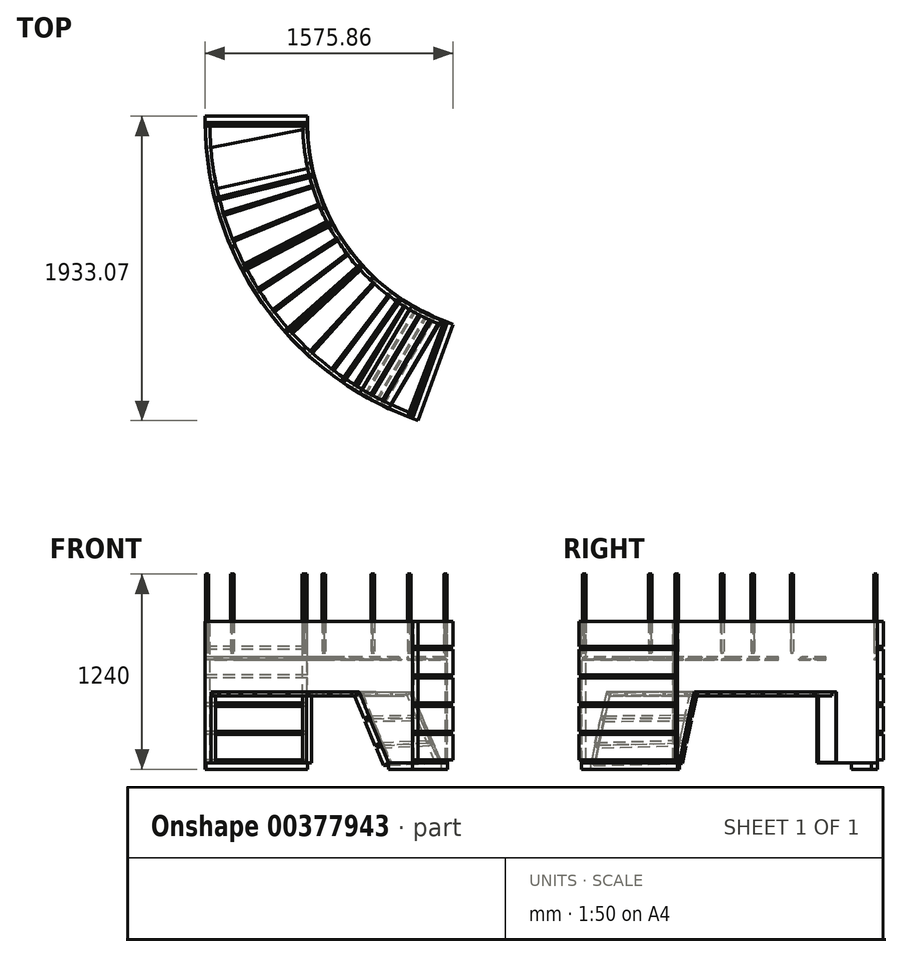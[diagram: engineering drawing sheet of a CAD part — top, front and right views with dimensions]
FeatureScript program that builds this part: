
annotation { "Feature Type Name" : "Feature", "Feature Type Description" : "" }
export const myFeature = defineFeature(function(context is Context, id is Id, definition is map)
    precondition{}
    {
        {
            var Q0;
            Q0=qCreatedBy(makeId("Front.planeOp"),FACE);
            var sketch = newSketch(context, id + "F0", { "sketchPlane" : qUnion([Q0])});
            skLineSegment(sketch, "E0", {"start": v(0, 0) * mm, "end": v(0, -500) * mm, "construction": true});
            skSolve(sketch);
        }
        {
            var Q0;
            Q0=qCreatedBy(makeId("Front.planeOp"),FACE);
            var sketch = newSketch(context, id + "F1", { "sketchPlane" : qUnion([Q0])});
            skLineSegment(sketch, "E1.bottom", {"start": v(-1350, 0) * mm, "end": v(-1380, 0) * mm});
            skLineSegment(sketch, "E1.top", {"start": v(-1350, 900) * mm, "end": v(-1380, 900) * mm});
            skLineSegment(sketch, "E1.left", {"start": v(-1350, 0) * mm, "end": v(-1350, 900) * mm});
            skLineSegment(sketch, "E1.right", {"start": v(-1380, 0) * mm, "end": v(-1380, 900) * mm});
            skLineSegment(sketch, "E2.bottom", {"start": v(-1970, 0) * mm, "end": v(-2000, 0) * mm});
            skLineSegment(sketch, "E2.top", {"start": v(-1970, 900) * mm, "end": v(-2000, 900) * mm});
            skLineSegment(sketch, "E2.left", {"start": v(-1970, 0) * mm, "end": v(-1970, 900) * mm});
            skLineSegment(sketch, "E2.right", {"start": v(-2000, 0) * mm, "end": v(-2000, 900) * mm});
            skSolve(sketch);
        }
        {
            var Q0;
            Q0=qCreatedBy(makeId("Top.planeOp"),FACE);
            var sketch = newSketch(context, id + "F2", { "sketchPlane" : qUnion([Q0])});
            skLineSegment(sketch, "E3", {"start": v(0, 0) * mm, "end": v(-461.73, -1268.59) * mm, "construction": true});
            skLineSegment(sketch, "E4", {"start": v(0, 0) * mm, "end": v(-1350, 0) * mm, "construction": true});
            skArc(sketch, "E5", {"start": v(-1350, 0) * mm, "mid": v(-1105.86, -774.33) * mm, "end": v(-461.73, -1268.59) * mm});
            skSolve(sketch);
        }
        {
            var Q0;
            Q0 = qSketchRegion(id + "F1", true);
            var Q1;
            Q1 = qConstructionFilter(qBodyType(qCreatedBy(id + "F2" ,EDGE), BodyType.WIRE), ConstructionObject.NO);
            sweep(context, id + "F3", {"profiles" : qUnion([Q0]), "path" : qUnion([Q1])});
        }
        {
            var Q0;
            Q0=qCreatedBy(makeId("Top.planeOp"),FACE);
            var sketch = newSketch(context, id + "F4", { "sketchPlane" : qUnion([Q0])});
            skLineSegment(sketch, "E6", {"start": v(0, 0) * mm, "end": v(-2454.07, -477.02) * mm});
            skLineSegment(sketch, "E7", {"start": v(-2454.07, -477.02) * mm, "end": v(-1287.6, -2142.92) * mm});
            skLineSegment(sketch, "E8", {"start": v(-1287.6, -2142.92) * mm, "end": v(0, 0) * mm});
            skSolve(sketch);
        }
        {
            var Q0;
            Q0 = qSketchRegion(id + "F4", true);
            extrude(context, id + "F5", {"entities" : qUnion([Q0]), "operationType" : NewBodyOperationType.REMOVE, "depth" : 450 * mm});
        }
        {
            var Q0;
            {var subQ0=sQuery(id+"F4.wireOp",EDGE,"E8");Q0=makeQuery(id+"F5.boolean.opBoolean","COPY",EDGE,{"disambiguationData":[topologyDisambiguationEdgeConnected([makeQuery(id+"F3.opSweep","SWEPT_FACE",FACE,{"disambiguationData":[OSD([sQuery(id+"F1.wireOp",EDGE,"E2.bottom"),sQuery(id+"F2.wireOp",EDGE,"E5")])]})])],"derivedFrom":makeQuery(id+"F5.opExtrude","CAP_EDGE",EDGE,{"disambiguationData":[OSD([subQ0])],"isStart":true})});}
            var Q1;
            {var subQ0=sQuery(id+"F4.wireOp",EDGE,"E8");Q1=makeQuery(id+"F5.boolean.opBoolean","COPY",EDGE,{"disambiguationData":[topologyDisambiguationEdgeConnected([makeQuery(id+"F3.opSweep","SWEPT_FACE",FACE,{"disambiguationData":[OSD([sQuery(id+"F1.wireOp",EDGE,"E1.bottom"),sQuery(id+"F2.wireOp",EDGE,"E5")])]})])],"derivedFrom":makeQuery(id+"F5.opExtrude","CAP_EDGE",EDGE,{"disambiguationData":[OSD([subQ0])],"isStart":true})});}
            var Q2;
            {var subQ0=sQuery(id+"F4.wireOp",EDGE,"E6");Q2=makeQuery(id+"F5.boolean.opBoolean","COPY",EDGE,{"disambiguationData":[topologyDisambiguationEdgeConnected([makeQuery(id+"F3.opSweep","SWEPT_FACE",FACE,{"disambiguationData":[OSD([sQuery(id+"F1.wireOp",EDGE,"E1.bottom"),sQuery(id+"F2.wireOp",EDGE,"E5")])]})])],"derivedFrom":makeQuery(id+"F5.opExtrude","CAP_EDGE",EDGE,{"disambiguationData":[OSD([subQ0])],"isStart":true})});}
            var Q3;
            {var subQ0=sQuery(id+"F4.wireOp",EDGE,"E6");Q3=makeQuery(id+"F5.boolean.opBoolean","COPY",EDGE,{"disambiguationData":[topologyDisambiguationEdgeConnected([makeQuery(id+"F3.opSweep","SWEPT_FACE",FACE,{"disambiguationData":[OSD([sQuery(id+"F1.wireOp",EDGE,"E2.bottom"),sQuery(id+"F2.wireOp",EDGE,"E5")])]})])],"derivedFrom":makeQuery(id+"F5.opExtrude","CAP_EDGE",EDGE,{"disambiguationData":[OSD([subQ0])],"isStart":true})});}
            chamfer(context, id + "F6", {"entities" : qUnion([Q0, Q1, Q2, Q3]), "chamferType" : ChamferType.OFFSET_ANGLE, "width" : 220 * mm, "oppositeDirection" : false, "angle" : 65 * degree, "tangentPropagation" : true});
        }
        {
            var Q0;
            Q0=makeQuery(id+"F3.opSweep","SWEPT_FACE",FACE,{"disambiguationData":[OSD([sQuery(id+"F1.wireOp",EDGE,"E2.left"),sQuery(id+"F2.wireOp",EDGE,"E5")])]});
            var Q1;
            Q1=makeQuery(id+"F3.opSweep","SWEPT_FACE",FACE,{"disambiguationData":[OSD([sQuery(id+"F1.wireOp",EDGE,"E2.top"),sQuery(id+"F2.wireOp",EDGE,"E5")])]});
            var Q2;
            Q2=makeQuery(id+"F3.opSweep","SWEPT_FACE",FACE,{"disambiguationData":[OSD([sQuery(id+"F1.wireOp",EDGE,"E1.right"),sQuery(id+"F2.wireOp",EDGE,"E5")])]});
            var Q3;
            Q3=makeQuery(id+"F3.opSweep","SWEPT_FACE",FACE,{"disambiguationData":[OSD([sQuery(id+"F1.wireOp",EDGE,"E1.top"),sQuery(id+"F2.wireOp",EDGE,"E5")])]});
            shell(context, id + "F7", {"entities" : qUnion([Q0, Q1, Q2, Q3]), "thickness" : 2.5 * mm});
        }
        {
            var Q0;
            {var subQ0=sQuery(id+"F2.wireOp",EDGE,"E5");var subQ1=sQuery(id+"F4.wireOp",EDGE,"E6");var subQ2=sQuery(id+"F4.wireOp",EDGE,"E8");Q0=makeQuery(id+"F5.boolean.opBoolean","COPY",FACE,{"disambiguationData":[TD([makeQuery(id+"F3.opSweep","SWEPT_FACE",FACE,{"disambiguationData":[OSD([sQuery(id+"F1.wireOp",EDGE,"E1.left"),subQ0])]})])],"derivedFrom":makeQuery(id+"F5.opExtrude","CAP_FACE",FACE,{"disambiguationData":[OSD([subQ1,sQuery(id+"F4.wireOp",EDGE,"E7"),subQ2])],"isStart":false})});}
            var Q1;
            Q1=makeQuery(id+"F3.opSweep","SWEPT_FACE",FACE,{"disambiguationData":[OSD([sQuery(id+"F1.wireOp",EDGE,"E1.top"),sQuery(id+"F2.wireOp",EDGE,"E5")])]});
            cPlane(context, id + "F8", {"entities" : qUnion([Q0, Q1]), "cplaneType" : CPlaneType.MID_PLANE, "offset" : 25 * mm, "width" : 150 * mm, "height" : 150 * mm});
        }
        {
            var Q0;
            Q0=qCreatedBy(id+"F8.planeOp",FACE);
            var sketch = newSketch(context, id + "F9", { "sketchPlane" : qUnion([Q0])});
            skLineSegment(sketch, "E9", {"start": v(-1352.5, 2.5) * mm, "end": v(-1997.5, 2.5) * mm});
            skLineSegment(sketch, "E10", {"start": v(-1997.5, 2.5) * mm, "end": v(-1997.5, 22.5) * mm});
            skLineSegment(sketch, "E11", {"start": v(-1997.5, 22.5) * mm, "end": v(-1352.5, 22.5) * mm});
            skLineSegment(sketch, "E12", {"start": v(-1352.5, 22.5) * mm, "end": v(-1352.5, 2.5) * mm});
            skSolve(sketch);
        }
        {
            var Q0;
            Q0 = qSketchRegion(id + "F9", true);
            extrude(context, id + "F10", {"entities" : qUnion([Q0]), "depth" : 20 * mm});
        }
        {
            var Q0;
            Q0=makeQuery(id+"F10.opExtrude","SWEPT_FACE",FACE,{"disambiguationData":[OSD([sQuery(id+"F9.wireOp",EDGE,"E11")])]});
            var Q1;
            Q1=makeQuery(id+"F10.opExtrude","CAP_FACE",FACE,{"disambiguationData":[OSD([sQuery(id+"F9.wireOp",EDGE,"E9"),sQuery(id+"F9.wireOp",EDGE,"E10"),sQuery(id+"F9.wireOp",EDGE,"E11"),sQuery(id+"F9.wireOp",EDGE,"E12")])],"isStart":true});
            var Q2;
            Q2=makeQuery(id+"F10.opExtrude","SWEPT_FACE",FACE,{"disambiguationData":[OSD([sQuery(id+"F9.wireOp",EDGE,"E10")])]});
            var Q3;
            Q3=makeQuery(id+"F10.opExtrude","SWEPT_FACE",FACE,{"disambiguationData":[OSD([sQuery(id+"F9.wireOp",EDGE,"E12")])]});
            shell(context, id + "F11", {"entities" : qUnion([Q0, Q1, Q2, Q3]), "thickness" : 5 * mm});
        }
        {
            var Q0;
            {var subQ0=sQuery(id+"F9.wireOp",EDGE,"E9");Q0=makeQuery(id+"F11.opShell","OFFSET_EDGE",EDGE,{"disambiguationData":[OSD([subQ0]),TDD([makeQuery(id+"F10.opExtrude","CAP_EDGE",EDGE,{"disambiguationData":[OSD([subQ0])],"isStart":false})])]});}
            var Q1;
            {var subQ0=sQuery(id+"F9.wireOp",EDGE,"E9");Q1=makeQuery(id+"F11.opShell","OFFSET_EDGE",EDGE,{"disambiguationData":[OSD([subQ0]),TDD([makeQuery(id+"F10.opExtrude","CAP_EDGE",EDGE,{"disambiguationData":[OSD([subQ0])],"isStart":true})])]});}
            var Q2;
            Q2=makeQuery(id+"F11.opShell","OFFSET_EDGE",EDGE,{"disambiguationData":[OSD([sQuery(id+"F9.wireOp",EDGE,"E11")])]});
            fillet(context, id + "F12", {"entities" : qUnion([Q0, Q1, Q2]), "radius" : 5 * mm, "tangentPropagation" : true, "allowEdgeOverflow" : false});
        }
        {
            var Q0;
            {var subQ0=sQuery(id+"F4.wireOp",EDGE,"E8");Q0=makeQuery(id+"F6.opChamfer","BLEND_FACE",FACE,{"disambiguationData":[OSD([subQ0]),TDD([makeQuery(id+"F5.boolean.opBoolean","COPY",EDGE,{"disambiguationData":[topologyDisambiguationEdgeConnected([makeQuery(id+"F3.opSweep","SWEPT_FACE",FACE,{"disambiguationData":[OSD([sQuery(id+"F1.wireOp",EDGE,"E1.bottom"),sQuery(id+"F2.wireOp",EDGE,"E5")])]})])],"derivedFrom":makeQuery(id+"F5.opExtrude","CAP_EDGE",EDGE,{"disambiguationData":[OSD([subQ0])],"isStart":true})})])]});}
            var sketch = newSketch(context, id + "F13", { "sketchPlane" : qUnion([Q0])});
            skLineSegment(sketch, "E13", {"start": v(1209.11, 723.39) * mm, "end": v(1840.7, 877.15) * mm});
            skLineSegment(sketch, "E14", {"start": v(1840.7, 877.15) * mm, "end": v(1878.54, 721.7) * mm});
            skLineSegment(sketch, "E15", {"start": v(1878.54, 721.7) * mm, "end": v(1246.35, 567.78) * mm});
            skLineSegment(sketch, "E16", {"start": v(1246.35, 567.78) * mm, "end": v(1209.11, 723.39) * mm});
            skLineSegment(sketch, "E17", {"start": v(1250.78, 548.28) * mm, "end": v(1284.28, 391.82) * mm});
            skLineSegment(sketch, "E18", {"start": v(1284.28, 391.82) * mm, "end": v(1920.62, 536.23) * mm});
            skLineSegment(sketch, "E19", {"start": v(1920.62, 536.23) * mm, "end": v(1882.96, 702.19) * mm});
            skLineSegment(sketch, "E20", {"start": v(1882.96, 702.19) * mm, "end": v(1250.78, 548.28) * mm});
            skLineSegment(sketch, "E21", {"start": v(1288.23, 372.22) * mm, "end": v(1924.58, 516.63) * mm});
            skLineSegment(sketch, "E22", {"start": v(1924.58, 516.63) * mm, "end": v(1951.13, 399.6) * mm});
            skLineSegment(sketch, "E23", {"start": v(1951.13, 399.6) * mm, "end": v(1314.79, 255.2) * mm});
            skLineSegment(sketch, "E24", {"start": v(1314.79, 255.2) * mm, "end": v(1288.23, 372.22) * mm});
            skSolve(sketch);
        }
        {
            var Q0;
            Q0 = qSketchRegion(id + "F13", true);
            extrude(context, id + "F14", {"entities" : qUnion([Q0]), "operationType" : NewBodyOperationType.ADD, "depth" : 40 * mm});
        }
        {
            var Q0;
            {var subQ2=sQuery(id+"F1.wireOp",EDGE,"E1.bottom");var subQ3=sQuery(id+"F2.wireOp",EDGE,"E5");Q0=makeQuery(id+"F5.boolean.opBoolean","SPLIT",FACE,{"disambiguationData":[TD([makeQuery(id+"F5.opExtrude","SWEPT_FACE",FACE,{"disambiguationData":[OSD([sQuery(id+"F4.wireOp",EDGE,"E8")])]})])],"derivedFrom":makeQuery(id+"F3.opSweep","SWEPT_FACE",FACE,{"disambiguationData":[OSD([subQ2,subQ3])]})});}
            var sketch = newSketch(context, id + "F15", { "sketchPlane" : qUnion([Q0])});
            skLineSegment(sketch, "E25", {"start": v(-497.43, 1255.02) * mm, "end": v(-461.73, 1268.59) * mm});
            skLineSegment(sketch, "E26", {"start": v(-461.73, 1268.59) * mm, "end": v(-684.04, 1879.39) * mm});
            skLineSegment(sketch, "E27", {"start": v(-684.04, 1879.39) * mm, "end": v(-835.25, 1817.24) * mm});
            skLineSegment(sketch, "E28", {"start": v(-835.25, 1817.24) * mm, "end": v(-497.43, 1255.02) * mm});
            skSolve(sketch);
        }
        {
            var Q0;
            Q0 = qSketchRegion(id + "F15", true);
            extrude(context, id + "F16", {"entities" : qUnion([Q0]), "depth" : 40 * mm});
        }
        {
            var Q0;
            Q0=makeQuery(id+"F3.opSweep","CAP_FACE",FACE,{"disambiguationData":[OSD([sQuery(id+"F1.wireOp",EDGE,"E1.bottom"),sQuery(id+"F1.wireOp",EDGE,"E1.top"),sQuery(id+"F1.wireOp",EDGE,"E1.left"),sQuery(id+"F1.wireOp",EDGE,"E1.right"),sQuery(id+"F2.wireOp",VERTEX,"E5.end")])],"isStart":false});
            var sketch = newSketch(context, id + "F17", { "sketchPlane" : qUnion([Q0])});
            skLineSegment(sketch, "E29.bottom", {"start": v(-1350, 900) * mm, "end": v(-2000, 900) * mm});
            skLineSegment(sketch, "E29.top", {"start": v(-1350, 740) * mm, "end": v(-2000, 740) * mm});
            skLineSegment(sketch, "E29.left", {"start": v(-1350, 900) * mm, "end": v(-1350, 740) * mm});
            skLineSegment(sketch, "E29.right", {"start": v(-2000, 900) * mm, "end": v(-2000, 740) * mm});
            skLineSegment(sketch, "E30.bottom", {"start": v(-1350, 720) * mm, "end": v(-2000, 720) * mm});
            skLineSegment(sketch, "E30.top", {"start": v(-1350, 560) * mm, "end": v(-2000, 560) * mm});
            skLineSegment(sketch, "E30.left", {"start": v(-1350, 720) * mm, "end": v(-1350, 560) * mm});
            skLineSegment(sketch, "E30.right", {"start": v(-2000, 720) * mm, "end": v(-2000, 560) * mm});
            skLineSegment(sketch, "E31.bottom", {"start": v(-1350, 540) * mm, "end": v(-2000, 540) * mm});
            skLineSegment(sketch, "E31.top", {"start": v(-1350, 380) * mm, "end": v(-2000, 380) * mm});
            skLineSegment(sketch, "E31.left", {"start": v(-1350, 540) * mm, "end": v(-1350, 380) * mm});
            skLineSegment(sketch, "E31.right", {"start": v(-2000, 540) * mm, "end": v(-2000, 380) * mm});
            skLineSegment(sketch, "E32.bottom", {"start": v(-1350, 360) * mm, "end": v(-2000, 360) * mm});
            skLineSegment(sketch, "E32.top", {"start": v(-1350, 200) * mm, "end": v(-2000, 200) * mm});
            skLineSegment(sketch, "E32.left", {"start": v(-1350, 360) * mm, "end": v(-1350, 200) * mm});
            skLineSegment(sketch, "E32.right", {"start": v(-2000, 360) * mm, "end": v(-2000, 200) * mm});
            skLineSegment(sketch, "E33.bottom", {"start": v(-1350, 180) * mm, "end": v(-2000, 180) * mm});
            skLineSegment(sketch, "E33.top", {"start": v(-1350, 20) * mm, "end": v(-2000, 20) * mm});
            skLineSegment(sketch, "E33.left", {"start": v(-1350, 180) * mm, "end": v(-1350, 20) * mm});
            skLineSegment(sketch, "E33.right", {"start": v(-2000, 180) * mm, "end": v(-2000, 20) * mm});
            skSolve(sketch);
        }
        {
            var Q0;
            {var subQ3=sQuery(id+"F17.wireOp",EDGE,"E29.right");Q0=makeQuery(id+"F17.imprint","IMPRINT",FACE,{"disambiguationData":[TD([[makeQuery(id+"F17.imprint","IMPRINT",EDGE,{"derivedFrom":subQ3}),1.0]])]});}
            var Q1;
            {var subQ0=sQuery(id+"F17.wireOp",EDGE,"E30.right");Q1=makeQuery(id+"F17.imprint","IMPRINT",FACE,{"disambiguationData":[TD([[makeQuery(id+"F17.imprint","IMPRINT",EDGE,{"derivedFrom":subQ0}),1.0]])]});}
            var Q2;
            {var subQ0=sQuery(id+"F17.wireOp",EDGE,"E31.right");Q2=makeQuery(id+"F17.imprint","IMPRINT",FACE,{"disambiguationData":[TD([[makeQuery(id+"F17.imprint","IMPRINT",EDGE,{"derivedFrom":subQ0}),1.0]])]});}
            var Q3;
            {var subQ0=sQuery(id+"F17.wireOp",EDGE,"E32.right");Q3=makeQuery(id+"F17.imprint","IMPRINT",FACE,{"disambiguationData":[TD([[makeQuery(id+"F17.imprint","IMPRINT",EDGE,{"derivedFrom":subQ0}),1.0]])]});}
            var Q4;
            {var subQ0=sQuery(id+"F17.wireOp",EDGE,"E29.left");Q4=makeQuery(id+"F17.imprint","IMPRINT",FACE,{"disambiguationData":[TD([[makeQuery(id+"F17.imprint","IMPRINT",EDGE,{"derivedFrom":subQ0}),1.0]])]});}
            var Q5;
            {var subQ0=sQuery(id+"F17.wireOp",EDGE,"E30.left");Q5=makeQuery(id+"F17.imprint","IMPRINT",FACE,{"disambiguationData":[TD([[makeQuery(id+"F17.imprint","IMPRINT",EDGE,{"derivedFrom":subQ0}),1.0]])]});}
            var Q6;
            {var subQ0=sQuery(id+"F17.wireOp",EDGE,"E31.left");Q6=makeQuery(id+"F17.imprint","IMPRINT",FACE,{"disambiguationData":[TD([[makeQuery(id+"F17.imprint","IMPRINT",EDGE,{"derivedFrom":subQ0}),1.0]])]});}
            var Q7;
            {var subQ0=sQuery(id+"F17.wireOp",EDGE,"E32.left");Q7=makeQuery(id+"F17.imprint","IMPRINT",FACE,{"disambiguationData":[TD([[makeQuery(id+"F17.imprint","IMPRINT",EDGE,{"derivedFrom":subQ0}),1.0]])]});}
            var Q8;
            {var subQ0=sQuery(id+"F17.wireOp",EDGE,"E33.left");Q8=makeQuery(id+"F17.imprint","IMPRINT",FACE,{"disambiguationData":[TD([[makeQuery(id+"F17.imprint","IMPRINT",EDGE,{"derivedFrom":subQ0}),1.0]])]});}
            var Q9;
            {var subQ0=sQuery(id+"F17.wireOp",EDGE,"E33.right");Q9=makeQuery(id+"F17.imprint","IMPRINT",FACE,{"disambiguationData":[TD([[makeQuery(id+"F17.imprint","IMPRINT",EDGE,{"derivedFrom":subQ0}),1.0]])]});}
            extrude(context, id + "F18", {"entities" : qUnion([Q0, Q1, Q2, Q3, Q4, Q5, Q6, Q7, Q8, Q9]), "depth" : 40 * mm});
        }
        {
            var Q0;
            Q0=makeQuery(id+"F3.opSweep","CAP_FACE",FACE,{"disambiguationData":[OSD([sQuery(id+"F1.wireOp",EDGE,"E1.bottom"),sQuery(id+"F1.wireOp",EDGE,"E1.top"),sQuery(id+"F1.wireOp",EDGE,"E1.left"),sQuery(id+"F1.wireOp",EDGE,"E1.right"),sQuery(id+"F2.wireOp",VERTEX,"E5.start")])],"isStart":true});
            var Q1;
            Q1=makeQuery(id+"F3.opSweep","CAP_FACE",FACE,{"disambiguationData":[OSD([sQuery(id+"F1.wireOp",EDGE,"E1.bottom"),sQuery(id+"F1.wireOp",EDGE,"E1.top"),sQuery(id+"F1.wireOp",EDGE,"E1.left"),sQuery(id+"F1.wireOp",EDGE,"E1.right"),sQuery(id+"F2.wireOp",VERTEX,"E5.end")])],"isStart":false});
            cPlane(context, id + "F19", {"entities" : qUnion([Q0, Q1]), "cplaneType" : CPlaneType.MID_PLANE, "offset" : 25 * mm, "width" : 150 * mm, "height" : 150 * mm});
        }
        {
            var Q0;
            {var subQ0=sQuery(id+"F2.wireOp",EDGE,"E5");var subQ1=sQuery(id+"F4.wireOp",EDGE,"E6");var subQ2=sQuery(id+"F4.wireOp",EDGE,"E8");Q0=makeQuery(id+"F5.boolean.opBoolean","COPY",FACE,{"disambiguationData":[TD([makeQuery(id+"F3.opSweep","SWEPT_FACE",FACE,{"disambiguationData":[OSD([sQuery(id+"F1.wireOp",EDGE,"E1.left"),subQ0])]})])],"derivedFrom":makeQuery(id+"F5.opExtrude","CAP_FACE",FACE,{"disambiguationData":[OSD([subQ1,sQuery(id+"F4.wireOp",EDGE,"E7"),subQ2])],"isStart":false})});}
            var sketch = newSketch(context, id + "F20", { "sketchPlane" : qUnion([Q0])});
            skLineSegment(sketch, "E34", {"start": v(-1068.25, 1690.81) * mm, "end": v(0, 0) * mm});
            skLineSegment(sketch, "E35", {"start": v(-1199.99, 1600) * mm, "end": v(0, 0) * mm});
            skLineSegment(sketch, "E36", {"start": v(-1215.93, 1587.93) * mm, "end": v(0, 0) * mm});
            skLineSegment(sketch, "E37", {"start": v(-1338.97, 1485.65) * mm, "end": v(0, 0) * mm});
            skLineSegment(sketch, "E38", {"start": v(-1199.99, 1600) * mm, "end": v(-1068.25, 1690.81) * mm});
            skLineSegment(sketch, "E39", {"start": v(-1338.97, 1485.65) * mm, "end": v(-1215.93, 1587.93) * mm});
            skLineSegment(sketch, "E40", {"start": v(0, 0) * mm, "end": v(-1353.76, 1472.19) * mm});
            skLineSegment(sketch, "E41", {"start": v(0, 0) * mm, "end": v(-1467.1, 1359.26) * mm});
            skLineSegment(sketch, "E42", {"start": v(0, 0) * mm, "end": v(-1480.63, 1344.52) * mm});
            skLineSegment(sketch, "E43", {"start": v(0, 0) * mm, "end": v(-1583.36, 1221.87) * mm});
            skLineSegment(sketch, "E44", {"start": v(0, 0) * mm, "end": v(-1595.5, 1205.97) * mm});
            skLineSegment(sketch, "E45", {"start": v(0, 0) * mm, "end": v(-1686.8, 1074.57) * mm});
            skLineSegment(sketch, "E46", {"start": v(-1353.76, 1472.19) * mm, "end": v(-1467.1, 1359.26) * mm});
            skLineSegment(sketch, "E47", {"start": v(-1480.63, 1344.52) * mm, "end": v(-1583.36, 1221.87) * mm});
            skLineSegment(sketch, "E48", {"start": v(-1595.5, 1205.97) * mm, "end": v(-1686.8, 1074.57) * mm});
            skLineSegment(sketch, "E49", {"start": v(-1353.76, 1472.19) * mm, "end": v(-1338.97, 1485.65) * mm, "construction": true});
            skLineSegment(sketch, "E50", {"start": v(-1467.1, 1359.26) * mm, "end": v(-1480.63, 1344.52) * mm, "construction": true});
            skLineSegment(sketch, "E51", {"start": v(-1583.36, 1221.87) * mm, "end": v(-1595.5, 1205.97) * mm, "construction": true});
            skLineSegment(sketch, "E52", {"start": v(-1215.93, 1587.93) * mm, "end": v(-1199.99, 1600) * mm, "construction": true});
            skSolve(sketch);
        }
        {
            var Q0;
            {var subQ0=sQuery(id+"F20.wireOp",EDGE,"E38");Q0=makeQuery(id+"F20.imprint","IMPRINT",FACE,{"disambiguationData":[TD([[makeQuery(id+"F20.imprint","IMPRINT",EDGE,{"derivedFrom":subQ0}),-1.0]])]});}
            var Q1;
            {var subQ0=sQuery(id+"F20.wireOp",EDGE,"E39");Q1=makeQuery(id+"F20.imprint","IMPRINT",FACE,{"disambiguationData":[TD([[makeQuery(id+"F20.imprint","IMPRINT",EDGE,{"derivedFrom":subQ0}),-1.0]])]});}
            var Q2;
            {var subQ0=sQuery(id+"F20.wireOp",EDGE,"E46");Q2=makeQuery(id+"F20.imprint","IMPRINT",FACE,{"disambiguationData":[TD([[makeQuery(id+"F20.imprint","IMPRINT",EDGE,{"derivedFrom":subQ0}),1.0]])]});}
            var Q3;
            {var subQ0=sQuery(id+"F20.wireOp",EDGE,"E47");Q3=makeQuery(id+"F20.imprint","IMPRINT",FACE,{"disambiguationData":[TD([[makeQuery(id+"F20.imprint","IMPRINT",EDGE,{"derivedFrom":subQ0}),1.0]])]});}
            var Q4;
            {var subQ0=sQuery(id+"F20.wireOp",EDGE,"E48");Q4=makeQuery(id+"F20.imprint","IMPRINT",FACE,{"disambiguationData":[TD([[makeQuery(id+"F20.imprint","IMPRINT",EDGE,{"derivedFrom":subQ0}),1.0]])]});}
            var Q5;
            {var subQ0=sQuery(id+"F20.wireOp",EDGE,"E34");var subQ1=makeQuery(id+"F5.opExtrude","CAP_FACE",FACE,{"disambiguationData":[OSD([sQuery(id+"F4.wireOp",EDGE,"E6"),sQuery(id+"F4.wireOp",EDGE,"E7"),sQuery(id+"F4.wireOp",EDGE,"E8")])],"isStart":false});var subQ2=sQuery(id+"F2.wireOp",EDGE,"E5");var subQ3=makeQuery(id+"F5.boolean.opBoolean","INTERSECT",EDGE,{"derivedFrom":[makeQuery(id+"F3.opSweep","SWEPT_FACE",FACE,{"disambiguationData":[OSD([sQuery(id+"F1.wireOp",EDGE,"E1.right"),subQ2])]}),subQ1]});var subQ4=makeQuery(id+"F20.imprint","INTERSECT",VERTEX,{"derivedFrom":[subQ3,subQ0]});Q5=makeQuery(id+"F20.imprint","IMPRINT",FACE,{"disambiguationData":[TD([[makeQuery(id+"F20.imprint","IMPRINT",EDGE,{"disambiguationData":[TD([[subQ4,-1.0]])],"derivedFrom":subQ0}),-1.0]])]});}
            var Q6;
            {var subQ0=sQuery(id+"F20.wireOp",EDGE,"E36");var subQ1=makeQuery(id+"F5.opExtrude","CAP_FACE",FACE,{"disambiguationData":[OSD([sQuery(id+"F4.wireOp",EDGE,"E6"),sQuery(id+"F4.wireOp",EDGE,"E7"),sQuery(id+"F4.wireOp",EDGE,"E8")])],"isStart":false});var subQ2=sQuery(id+"F2.wireOp",EDGE,"E5");var subQ3=makeQuery(id+"F5.boolean.opBoolean","INTERSECT",EDGE,{"derivedFrom":[makeQuery(id+"F3.opSweep","SWEPT_FACE",FACE,{"disambiguationData":[OSD([sQuery(id+"F1.wireOp",EDGE,"E1.right"),subQ2])]}),subQ1]});var subQ4=makeQuery(id+"F20.imprint","INTERSECT",VERTEX,{"derivedFrom":[subQ3,subQ0]});Q6=makeQuery(id+"F20.imprint","IMPRINT",FACE,{"disambiguationData":[TD([[makeQuery(id+"F20.imprint","IMPRINT",EDGE,{"disambiguationData":[TD([[subQ4,-1.0]])],"derivedFrom":subQ0}),-1.0]])]});}
            var Q7;
            {var subQ0=sQuery(id+"F20.wireOp",EDGE,"E40");var subQ1=makeQuery(id+"F5.opExtrude","CAP_FACE",FACE,{"disambiguationData":[OSD([sQuery(id+"F4.wireOp",EDGE,"E6"),sQuery(id+"F4.wireOp",EDGE,"E7"),sQuery(id+"F4.wireOp",EDGE,"E8")])],"isStart":false});var subQ2=sQuery(id+"F2.wireOp",EDGE,"E5");var subQ3=makeQuery(id+"F5.boolean.opBoolean","INTERSECT",EDGE,{"derivedFrom":[makeQuery(id+"F3.opSweep","SWEPT_FACE",FACE,{"disambiguationData":[OSD([sQuery(id+"F1.wireOp",EDGE,"E1.right"),subQ2])]}),subQ1]});var subQ4=makeQuery(id+"F20.imprint","INTERSECT",VERTEX,{"derivedFrom":[subQ3,subQ0]});Q7=makeQuery(id+"F20.imprint","IMPRINT",FACE,{"disambiguationData":[TD([[makeQuery(id+"F20.imprint","IMPRINT",EDGE,{"disambiguationData":[TD([[subQ4,1.0]])],"derivedFrom":subQ0}),1.0]])]});}
            var Q8;
            {var subQ0=sQuery(id+"F20.wireOp",EDGE,"E42");var subQ1=makeQuery(id+"F5.opExtrude","CAP_FACE",FACE,{"disambiguationData":[OSD([sQuery(id+"F4.wireOp",EDGE,"E6"),sQuery(id+"F4.wireOp",EDGE,"E7"),sQuery(id+"F4.wireOp",EDGE,"E8")])],"isStart":false});var subQ2=sQuery(id+"F2.wireOp",EDGE,"E5");var subQ3=makeQuery(id+"F5.boolean.opBoolean","INTERSECT",EDGE,{"derivedFrom":[makeQuery(id+"F3.opSweep","SWEPT_FACE",FACE,{"disambiguationData":[OSD([sQuery(id+"F1.wireOp",EDGE,"E1.right"),subQ2])]}),subQ1]});var subQ4=makeQuery(id+"F20.imprint","INTERSECT",VERTEX,{"derivedFrom":[subQ3,subQ0]});Q8=makeQuery(id+"F20.imprint","IMPRINT",FACE,{"disambiguationData":[TD([[makeQuery(id+"F20.imprint","IMPRINT",EDGE,{"disambiguationData":[TD([[subQ4,1.0]])],"derivedFrom":subQ0}),1.0]])]});}
            var Q9;
            {var subQ0=sQuery(id+"F20.wireOp",EDGE,"E44");var subQ1=makeQuery(id+"F5.opExtrude","CAP_FACE",FACE,{"disambiguationData":[OSD([sQuery(id+"F4.wireOp",EDGE,"E6"),sQuery(id+"F4.wireOp",EDGE,"E7"),sQuery(id+"F4.wireOp",EDGE,"E8")])],"isStart":false});var subQ2=sQuery(id+"F2.wireOp",EDGE,"E5");var subQ3=makeQuery(id+"F5.boolean.opBoolean","INTERSECT",EDGE,{"derivedFrom":[makeQuery(id+"F3.opSweep","SWEPT_FACE",FACE,{"disambiguationData":[OSD([sQuery(id+"F1.wireOp",EDGE,"E1.right"),subQ2])]}),subQ1]});var subQ4=makeQuery(id+"F20.imprint","INTERSECT",VERTEX,{"derivedFrom":[subQ3,subQ0]});Q9=makeQuery(id+"F20.imprint","IMPRINT",FACE,{"disambiguationData":[TD([[makeQuery(id+"F20.imprint","IMPRINT",EDGE,{"disambiguationData":[TD([[subQ4,1.0]])],"derivedFrom":subQ0}),1.0]])]});}
            extrude(context, id + "F21", {"entities" : qUnion([Q0, Q1, Q2, Q3, Q4, Q5, Q6, Q7, Q8, Q9]), "depth" : 25 * mm});
        }
        {
            var Q0;
            Q0=makeQuery(id+"F21.opExtrude","SWEPT_BODY",BODY,{"disambiguationData":[OSD([sQuery(id+"F1.wireOp",EDGE,"E1.left"),sQuery(id+"F2.wireOp",EDGE,"E5"),sQuery(id+"F4.wireOp",EDGE,"E6"),sQuery(id+"F4.wireOp",EDGE,"E7"),sQuery(id+"F4.wireOp",EDGE,"E8"),sQuery(id+"F20.wireOp",EDGE,"E44"),sQuery(id+"F20.wireOp",EDGE,"E45"),sQuery(id+"F20.wireOp",EDGE,"E48")])]});
            var Q1;
            Q1=makeQuery(id+"F21.opExtrude","SWEPT_BODY",BODY,{"disambiguationData":[OSD([sQuery(id+"F1.wireOp",EDGE,"E1.left"),sQuery(id+"F2.wireOp",EDGE,"E5"),sQuery(id+"F4.wireOp",EDGE,"E6"),sQuery(id+"F4.wireOp",EDGE,"E7"),sQuery(id+"F4.wireOp",EDGE,"E8"),sQuery(id+"F20.wireOp",EDGE,"E42"),sQuery(id+"F20.wireOp",EDGE,"E43"),sQuery(id+"F20.wireOp",EDGE,"E47")])]});
            var Q2;
            Q2=makeQuery(id+"F21.opExtrude","SWEPT_BODY",BODY,{"disambiguationData":[OSD([sQuery(id+"F1.wireOp",EDGE,"E1.left"),sQuery(id+"F2.wireOp",EDGE,"E5"),sQuery(id+"F4.wireOp",EDGE,"E6"),sQuery(id+"F4.wireOp",EDGE,"E7"),sQuery(id+"F4.wireOp",EDGE,"E8"),sQuery(id+"F20.wireOp",EDGE,"E40"),sQuery(id+"F20.wireOp",EDGE,"E41"),sQuery(id+"F20.wireOp",EDGE,"E46")])]});
            var Q3;
            Q3=makeQuery(id+"F21.opExtrude","SWEPT_BODY",BODY,{"disambiguationData":[OSD([sQuery(id+"F1.wireOp",EDGE,"E1.left"),sQuery(id+"F2.wireOp",EDGE,"E5"),sQuery(id+"F4.wireOp",EDGE,"E6"),sQuery(id+"F4.wireOp",EDGE,"E7"),sQuery(id+"F4.wireOp",EDGE,"E8"),sQuery(id+"F20.wireOp",EDGE,"E36"),sQuery(id+"F20.wireOp",EDGE,"E37"),sQuery(id+"F20.wireOp",EDGE,"E39")])]});
            var Q4;
            Q4=makeQuery(id+"F21.opExtrude","SWEPT_BODY",BODY,{"disambiguationData":[OSD([sQuery(id+"F1.wireOp",EDGE,"E1.left"),sQuery(id+"F2.wireOp",EDGE,"E5"),sQuery(id+"F4.wireOp",EDGE,"E6"),sQuery(id+"F4.wireOp",EDGE,"E7"),sQuery(id+"F4.wireOp",EDGE,"E8"),sQuery(id+"F20.wireOp",EDGE,"E34"),sQuery(id+"F20.wireOp",EDGE,"E35"),sQuery(id+"F20.wireOp",EDGE,"E38")])]});
            var Q5;
            Q5=makeQuery(id+"F3.opSweep","SWEPT_BODY",BODY,{"disambiguationData":[OSD([sQuery(id+"F1.wireOp",EDGE,"E2.bottom"),sQuery(id+"F1.wireOp",EDGE,"E2.top"),sQuery(id+"F1.wireOp",EDGE,"E2.left"),sQuery(id+"F1.wireOp",EDGE,"E2.right"),sQuery(id+"F2.wireOp",EDGE,"E5")])]});
            var Q6;
            Q6=makeQuery(id+"F16.opExtrude","SWEPT_BODY",BODY,{"disambiguationData":[OSD([sQuery(id+"F15.wireOp",EDGE,"E25"),sQuery(id+"F15.wireOp",EDGE,"E26"),sQuery(id+"F15.wireOp",EDGE,"E27"),sQuery(id+"F15.wireOp",EDGE,"E28")])]});
            var Q7;
            Q7=makeQuery(id+"F18.opExtrude","SWEPT_BODY",BODY,{"disambiguationData":[OSD([sQuery(id+"F17.wireOp",EDGE,"E33.bottom"),sQuery(id+"F17.wireOp",EDGE,"E33.top"),sQuery(id+"F17.wireOp",EDGE,"E33.left"),sQuery(id+"F17.wireOp",EDGE,"E33.right")])]});
            var Q8;
            Q8=makeQuery(id+"F18.opExtrude","SWEPT_BODY",BODY,{"disambiguationData":[OSD([sQuery(id+"F17.wireOp",EDGE,"E32.bottom"),sQuery(id+"F17.wireOp",EDGE,"E32.top"),sQuery(id+"F17.wireOp",EDGE,"E32.left"),sQuery(id+"F17.wireOp",EDGE,"E32.right")])]});
            var Q9;
            Q9=makeQuery(id+"F18.opExtrude","SWEPT_BODY",BODY,{"disambiguationData":[OSD([sQuery(id+"F17.wireOp",EDGE,"E31.bottom"),sQuery(id+"F17.wireOp",EDGE,"E31.top"),sQuery(id+"F17.wireOp",EDGE,"E31.left"),sQuery(id+"F17.wireOp",EDGE,"E31.right")])]});
            var Q10;
            Q10=makeQuery(id+"F18.opExtrude","SWEPT_BODY",BODY,{"disambiguationData":[OSD([sQuery(id+"F17.wireOp",EDGE,"E30.bottom"),sQuery(id+"F17.wireOp",EDGE,"E30.top"),sQuery(id+"F17.wireOp",EDGE,"E30.left"),sQuery(id+"F17.wireOp",EDGE,"E30.right")])]});
            var Q11;
            Q11=makeQuery(id+"F18.opExtrude","SWEPT_BODY",BODY,{"disambiguationData":[OSD([sQuery(id+"F17.wireOp",EDGE,"E29.bottom"),sQuery(id+"F17.wireOp",EDGE,"E29.top"),sQuery(id+"F17.wireOp",EDGE,"E29.left"),sQuery(id+"F17.wireOp",EDGE,"E29.right")])]});
            var Q12;
            Q12=qCreatedBy(id+"F19.planeOp",FACE);
            mirror(context, id + "F22", {"entities" : qUnion([Q0, Q1, Q2, Q3, Q4, Q5, Q6, Q7, Q8, Q9, Q10, Q11]), "mirrorPlane" : qUnion([Q12])});
        }
        {
            var Q0;
            Q0=makeQuery(id+"F10.opExtrude","SWEPT_BODY",BODY,{"disambiguationData":[OSD([sQuery(id+"F9.wireOp",EDGE,"E9"),sQuery(id+"F9.wireOp",EDGE,"E10"),sQuery(id+"F9.wireOp",EDGE,"E11"),sQuery(id+"F9.wireOp",EDGE,"E12")])]});
            var Q1;
            Q1=sQuery(id+"F0.wireOp",EDGE,"E0");
            circularPattern(context, id + "F23", {"entities" : qUnion([Q0]), "axis" : qUnion([Q1]), "angle" : 69 * degree, "instanceCount" : 6, "oppositeDirection" : true, "equalSpace" : true});
        }
        {
            var Q0;
            Q0=makeQuery(id+"F3.opSweep","SWEPT_FACE",FACE,{"disambiguationData":[OSD([sQuery(id+"F1.wireOp",EDGE,"E1.top"),sQuery(id+"F2.wireOp",EDGE,"E5")])]});
            var sketch = newSketch(context, id + "F24", { "sketchPlane" : qUnion([Q0])});
            skLineSegment(sketch, "E53", {"start": v(-1352.5, -2.5) * mm, "end": v(-1352.31, -22.5) * mm});
            skLineSegment(sketch, "E54", {"start": v(-1352.31, -22.5) * mm, "end": v(-1357.31, -22.5) * mm});
            skLineSegment(sketch, "E55", {"start": v(-1357.31, -22.5) * mm, "end": v(-1357.31, -15) * mm});
            skLineSegment(sketch, "E56", {"start": v(-1357.31, -15) * mm, "end": v(-1372.5, -15) * mm});
            skLineSegment(sketch, "E57", {"start": v(-1372.5, -15) * mm, "end": v(-1372.5, -10) * mm});
            skLineSegment(sketch, "E58", {"start": v(-1372.5, -10) * mm, "end": v(-1357.5, -10) * mm});
            skLineSegment(sketch, "E59", {"start": v(-1357.5, -10) * mm, "end": v(-1357.5, -2.5) * mm});
            skLineSegment(sketch, "E60", {"start": v(-1357.5, -2.5) * mm, "end": v(-1352.5, -2.5) * mm});
            skLineSegment(sketch, "E61", {"start": v(-1997.5, -22.5) * mm, "end": v(-1997.5, -2.5) * mm});
            skLineSegment(sketch, "E62", {"start": v(-1997.5, -2.5) * mm, "end": v(-1992.5, -2.5) * mm});
            skLineSegment(sketch, "E63", {"start": v(-1992.5, -2.5) * mm, "end": v(-1992.5, -10) * mm});
            skLineSegment(sketch, "E64", {"start": v(-1992.5, -10) * mm, "end": v(-1977.5, -10) * mm});
            skLineSegment(sketch, "E65", {"start": v(-1977.5, -10) * mm, "end": v(-1977.5, -15) * mm});
            skLineSegment(sketch, "E66", {"start": v(-1977.5, -15) * mm, "end": v(-1992.5, -15) * mm});
            skLineSegment(sketch, "E67", {"start": v(-1992.5, -15) * mm, "end": v(-1992.5, -22.5) * mm});
            skLineSegment(sketch, "E68", {"start": v(-1992.5, -22.5) * mm, "end": v(-1997.5, -22.5) * mm});
            skSolve(sketch);
        }
        {
            var Q0;
            Q0 = qSketchRegion(id + "F24", true);
            extrude(context, id + "F25", {"entities" : qUnion([Q0]), "depth" : 300 * mm, "hasSecondDirection" : true, "secondDirectionOppositeDirection" : true, "secondDirectionDepth" : 200 * mm});
        }
        {
            var Q0;
            Q0=makeQuery(id+"F25.opExtrude","SWEPT_EDGE",EDGE,{"disambiguationData":[OSD([sQuery(id+"F24.wireOp",EDGE,"E55"),sQuery(id+"F24.wireOp",EDGE,"E56")])]});
            var Q1;
            Q1=makeQuery(id+"F25.opExtrude","SWEPT_EDGE",EDGE,{"disambiguationData":[OSD([sQuery(id+"F24.wireOp",EDGE,"E54"),sQuery(id+"F24.wireOp",EDGE,"E55")])]});
            var Q2;
            Q2=makeQuery(id+"F25.opExtrude","SWEPT_EDGE",EDGE,{"disambiguationData":[OSD([sQuery(id+"F24.wireOp",EDGE,"E58"),sQuery(id+"F24.wireOp",EDGE,"E59")])]});
            var Q3;
            Q3=makeQuery(id+"F25.opExtrude","SWEPT_EDGE",EDGE,{"disambiguationData":[OSD([sQuery(id+"F1.wireOp",EDGE,"E1.top"),sQuery(id+"F2.wireOp",VERTEX,"E5.start"),sQuery(id+"F24.wireOp",EDGE,"E59"),sQuery(id+"F24.wireOp",EDGE,"E60")])]});
            var Q4;
            Q4=makeQuery(id+"F25.opExtrude","SWEPT_EDGE",EDGE,{"disambiguationData":[OSD([sQuery(id+"F24.wireOp",EDGE,"E57"),sQuery(id+"F24.wireOp",EDGE,"E58")])]});
            var Q5;
            Q5=makeQuery(id+"F25.opExtrude","SWEPT_EDGE",EDGE,{"disambiguationData":[OSD([sQuery(id+"F24.wireOp",EDGE,"E56"),sQuery(id+"F24.wireOp",EDGE,"E57")])]});
            var Q6;
            Q6=makeQuery(id+"F25.opExtrude","SWEPT_EDGE",EDGE,{"disambiguationData":[OSD([sQuery(id+"F24.wireOp",EDGE,"E66"),sQuery(id+"F24.wireOp",EDGE,"E67")])]});
            var Q7;
            Q7=makeQuery(id+"F25.opExtrude","SWEPT_EDGE",EDGE,{"disambiguationData":[OSD([sQuery(id+"F24.wireOp",EDGE,"E65"),sQuery(id+"F24.wireOp",EDGE,"E66")])]});
            var Q8;
            Q8=makeQuery(id+"F25.opExtrude","SWEPT_EDGE",EDGE,{"disambiguationData":[OSD([sQuery(id+"F24.wireOp",EDGE,"E64"),sQuery(id+"F24.wireOp",EDGE,"E65")])]});
            var Q9;
            Q9=makeQuery(id+"F25.opExtrude","SWEPT_EDGE",EDGE,{"disambiguationData":[OSD([sQuery(id+"F24.wireOp",EDGE,"E67"),sQuery(id+"F24.wireOp",EDGE,"E68")])]});
            var Q10;
            Q10=makeQuery(id+"F25.opExtrude","SWEPT_EDGE",EDGE,{"disambiguationData":[OSD([sQuery(id+"F24.wireOp",EDGE,"E63"),sQuery(id+"F24.wireOp",EDGE,"E64")])]});
            var Q11;
            Q11=makeQuery(id+"F25.opExtrude","SWEPT_EDGE",EDGE,{"disambiguationData":[OSD([sQuery(id+"F24.wireOp",EDGE,"E62"),sQuery(id+"F24.wireOp",EDGE,"E63")])]});
            fillet(context, id + "F26", {"entities" : qUnion([Q0, Q1, Q2, Q3, Q4, Q5, Q6, Q7, Q8, Q9, Q10, Q11]), "radius" : 2 * mm, "tangentPropagation" : true, "allowEdgeOverflow" : false});
        }
        {
            var Q0;
            Q0=makeQuery(id+"F25.opExtrude","SWEPT_BODY",BODY,{"disambiguationData":[OSD([sQuery(id+"F24.wireOp",EDGE,"E53"),sQuery(id+"F24.wireOp",EDGE,"E54"),sQuery(id+"F24.wireOp",EDGE,"E55"),sQuery(id+"F24.wireOp",EDGE,"E56"),sQuery(id+"F24.wireOp",EDGE,"E57"),sQuery(id+"F24.wireOp",EDGE,"E58"),sQuery(id+"F24.wireOp",EDGE,"E59"),sQuery(id+"F24.wireOp",EDGE,"E60")])]});
            var Q1;
            Q1=makeQuery(id+"F25.opExtrude","SWEPT_BODY",BODY,{"disambiguationData":[OSD([sQuery(id+"F24.wireOp",EDGE,"E61"),sQuery(id+"F24.wireOp",EDGE,"E62"),sQuery(id+"F24.wireOp",EDGE,"E63"),sQuery(id+"F24.wireOp",EDGE,"E64"),sQuery(id+"F24.wireOp",EDGE,"E65"),sQuery(id+"F24.wireOp",EDGE,"E66"),sQuery(id+"F24.wireOp",EDGE,"E67"),sQuery(id+"F24.wireOp",EDGE,"E68")])]});
            var Q2;
            Q2=sQuery(id+"F0.wireOp",EDGE,"E0");
            circularPattern(context, id + "F27", {"entities" : qUnion([Q0, Q1]), "axis" : qUnion([Q2]), "angle" : 69 * degree, "instanceCount" : 4, "oppositeDirection" : true, "equalSpace" : true});
        }
    });
